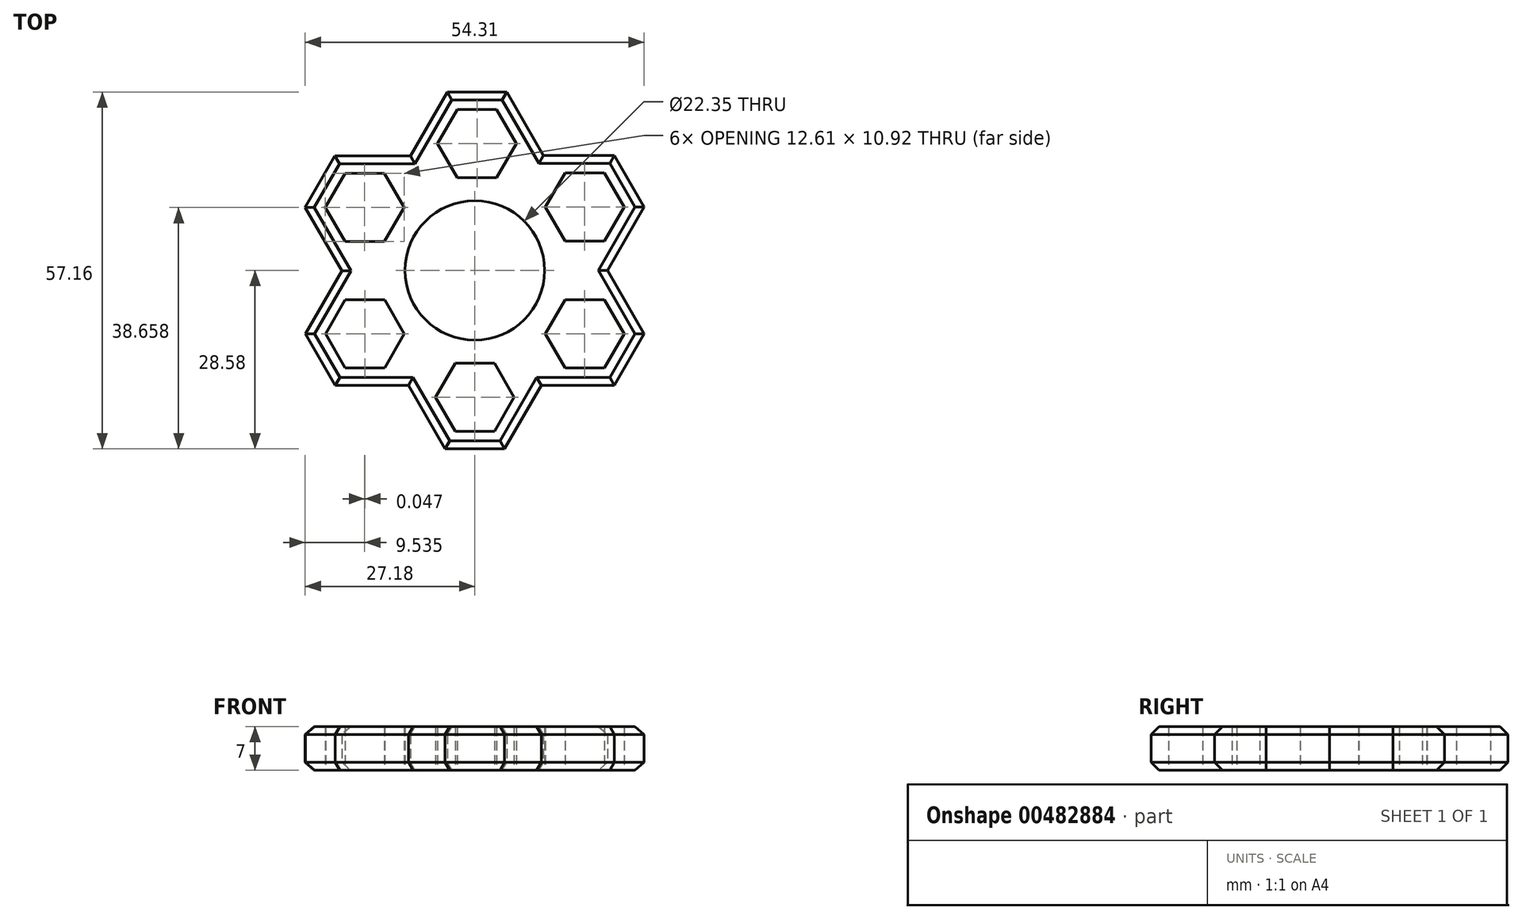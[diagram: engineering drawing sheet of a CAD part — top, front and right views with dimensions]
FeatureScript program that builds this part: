
annotation { "Feature Type Name" : "Feature", "Feature Type Description" : "" }
export const myFeature = defineFeature(function(context is Context, id is Id, definition is map)
    precondition{}
    {
        {
            var Q0;
            Q0=qCreatedBy(makeId("Top.planeOp"),FACE);
            var sketch = newSketch(context, id + "F0", { "sketchPlane" : qUnion([Q0])});
            skCircle(sketch, "E0", {"center": v(0, 0) * mm, "radius": 10.95 * mm});
            skCircle(sketch, "E1.cCircle", {"center": v(0, 0) * mm, "radius": 12.7 * mm, "construction": true});
            skLineSegment(sketch, "E1.0", {"start": v(-7.33, 12.7) * mm, "end": v(7.33, 12.7) * mm});
            skLineSegment(sketch, "E1.1", {"start": v(7.33, 12.7) * mm, "end": v(14.66, 0) * mm});
            skLineSegment(sketch, "E1.2", {"start": v(14.66, 0) * mm, "end": v(7.33, -12.7) * mm});
            skLineSegment(sketch, "E1.3", {"start": v(7.33, -12.7) * mm, "end": v(-7.33, -12.7) * mm});
            skLineSegment(sketch, "E1.4", {"start": v(-7.33, -12.7) * mm, "end": v(-14.66, 0) * mm});
            skLineSegment(sketch, "E1.5", {"start": v(-14.66, 0) * mm, "end": v(-7.33, 12.7) * mm});
            skPoint(sketch, "E1.0.midPoint", {"position": v(0, 12.7) * mm});
            skPoint(sketch, "E2.endSnap0", {"position": v(0, -12.7) * mm});
            skCircle(sketch, "E3.cCircle", {"center": v(0.35, 20.32) * mm, "radius": 5.46 * mm, "construction": true});
            skLineSegment(sketch, "E3.0", {"start": v(3.5, 14.86) * mm, "end": v(-2.8, 14.86) * mm});
            skLineSegment(sketch, "E3.1", {"start": v(-2.8, 14.86) * mm, "end": v(-5.95, 20.32) * mm});
            skLineSegment(sketch, "E3.2", {"start": v(-5.95, 20.32) * mm, "end": v(-2.8, 25.78) * mm});
            skLineSegment(sketch, "E3.3", {"start": v(-2.8, 25.78) * mm, "end": v(3.5, 25.78) * mm});
            skLineSegment(sketch, "E3.4", {"start": v(3.5, 25.78) * mm, "end": v(6.66, 20.32) * mm});
            skLineSegment(sketch, "E3.5", {"start": v(6.66, 20.32) * mm, "end": v(3.5, 14.86) * mm});
            skPoint(sketch, "E3.0.midPoint", {"position": v(0.35, 14.86) * mm});
            skCircle(sketch, "E4.cCircle", {"center": v(17.6, 10.16) * mm, "radius": 5.46 * mm, "construction": true});
            skLineSegment(sketch, "E4.0", {"start": v(14.44, 4.7) * mm, "end": v(11.3, 10.16) * mm});
            skLineSegment(sketch, "E4.1", {"start": v(11.3, 10.16) * mm, "end": v(14.44, 15.62) * mm});
            skLineSegment(sketch, "E4.2", {"start": v(14.44, 15.62) * mm, "end": v(20.75, 15.62) * mm});
            skLineSegment(sketch, "E4.3", {"start": v(20.75, 15.62) * mm, "end": v(23.9, 10.16) * mm});
            skLineSegment(sketch, "E4.4", {"start": v(23.9, 10.16) * mm, "end": v(20.75, 4.7) * mm});
            skLineSegment(sketch, "E4.5", {"start": v(20.75, 4.7) * mm, "end": v(14.44, 4.7) * mm});
            skPoint(sketch, "E4.0.midPoint", {"position": v(12.87, 7.43) * mm});
            skCircle(sketch, "E5.cCircle", {"center": v(17.6, -10.16) * mm, "radius": 5.46 * mm, "construction": true});
            skLineSegment(sketch, "E5.0", {"start": v(11.3, -10.16) * mm, "end": v(14.44, -4.7) * mm});
            skLineSegment(sketch, "E5.1", {"start": v(14.44, -4.7) * mm, "end": v(20.75, -4.7) * mm});
            skLineSegment(sketch, "E5.2", {"start": v(20.75, -4.7) * mm, "end": v(23.9, -10.16) * mm});
            skLineSegment(sketch, "E5.3", {"start": v(23.9, -10.16) * mm, "end": v(20.75, -15.62) * mm});
            skLineSegment(sketch, "E5.4", {"start": v(20.75, -15.62) * mm, "end": v(14.44, -15.62) * mm});
            skLineSegment(sketch, "E5.5", {"start": v(14.44, -15.62) * mm, "end": v(11.3, -10.16) * mm});
            skPoint(sketch, "E5.0.midPoint", {"position": v(12.87, -7.43) * mm});
            skCircle(sketch, "E6.cCircle", {"center": v(0, -20.32) * mm, "radius": 5.46 * mm, "construction": true});
            skLineSegment(sketch, "E6.0", {"start": v(-3.15, -14.86) * mm, "end": v(3.15, -14.86) * mm});
            skLineSegment(sketch, "E6.1", {"start": v(3.15, -14.86) * mm, "end": v(6.3, -20.32) * mm});
            skLineSegment(sketch, "E6.2", {"start": v(6.3, -20.32) * mm, "end": v(3.15, -25.78) * mm});
            skLineSegment(sketch, "E6.3", {"start": v(3.15, -25.78) * mm, "end": v(-3.15, -25.78) * mm});
            skLineSegment(sketch, "E6.4", {"start": v(-3.15, -25.78) * mm, "end": v(-6.3, -20.32) * mm});
            skLineSegment(sketch, "E6.5", {"start": v(-6.3, -20.32) * mm, "end": v(-3.15, -14.86) * mm});
            skPoint(sketch, "E6.0.midPoint", {"position": v(0, -14.86) * mm});
            skCircle(sketch, "E7.cCircle", {"center": v(-17.6, -10.16) * mm, "radius": 5.46 * mm, "construction": true});
            skLineSegment(sketch, "E7.0", {"start": v(-14.44, -4.7) * mm, "end": v(-11.3, -10.16) * mm});
            skLineSegment(sketch, "E7.1", {"start": v(-11.3, -10.16) * mm, "end": v(-14.44, -15.62) * mm});
            skLineSegment(sketch, "E7.2", {"start": v(-14.44, -15.62) * mm, "end": v(-20.75, -15.62) * mm});
            skLineSegment(sketch, "E7.3", {"start": v(-20.75, -15.62) * mm, "end": v(-23.9, -10.16) * mm});
            skLineSegment(sketch, "E7.4", {"start": v(-23.9, -10.16) * mm, "end": v(-20.75, -4.7) * mm});
            skLineSegment(sketch, "E7.5", {"start": v(-20.75, -4.7) * mm, "end": v(-14.44, -4.7) * mm});
            skPoint(sketch, "E7.0.midPoint", {"position": v(-12.87, -7.43) * mm});
            skCircle(sketch, "E8.cCircle", {"center": v(-17.64, 10.08) * mm, "radius": 5.46 * mm, "construction": true});
            skLineSegment(sketch, "E8.0", {"start": v(-11.34, 10.08) * mm, "end": v(-14.5, 4.62) * mm});
            skLineSegment(sketch, "E8.1", {"start": v(-14.5, 4.62) * mm, "end": v(-20.8, 4.62) * mm});
            skLineSegment(sketch, "E8.2", {"start": v(-20.8, 4.62) * mm, "end": v(-23.95, 10.08) * mm});
            skLineSegment(sketch, "E8.3", {"start": v(-23.95, 10.08) * mm, "end": v(-20.8, 15.54) * mm});
            skLineSegment(sketch, "E8.4", {"start": v(-20.8, 15.54) * mm, "end": v(-14.5, 15.54) * mm});
            skLineSegment(sketch, "E8.5", {"start": v(-14.5, 15.54) * mm, "end": v(-11.34, 10.08) * mm});
            skPoint(sketch, "E8.0.midPoint", {"position": v(-12.92, 7.35) * mm});
            skCircle(sketch, "E9.cCircle", {"center": v(-17.64, 10.08) * mm, "radius": 8.26 * mm, "construction": true});
            skLineSegment(sketch, "E9.0", {"start": v(-8.11, 10.08) * mm, "end": v(-12.88, 1.82) * mm});
            skLineSegment(sketch, "E9.1", {"start": v(-12.88, 1.82) * mm, "end": v(-22.41, 1.82) * mm});
            skLineSegment(sketch, "E9.2", {"start": v(-22.41, 1.82) * mm, "end": v(-27.18, 10.08) * mm});
            skLineSegment(sketch, "E9.3", {"start": v(-27.18, 10.08) * mm, "end": v(-22.41, 18.33) * mm});
            skLineSegment(sketch, "E9.4", {"start": v(-22.41, 18.33) * mm, "end": v(-12.88, 18.33) * mm});
            skLineSegment(sketch, "E9.5", {"start": v(-12.88, 18.33) * mm, "end": v(-8.11, 10.08) * mm});
            skPoint(sketch, "E9.0.midPoint", {"position": v(-10.5, 5.95) * mm});
            skCircle(sketch, "E10.cCircle", {"center": v(0.35, 20.32) * mm, "radius": 8.26 * mm, "construction": true});
            skLineSegment(sketch, "E10.0", {"start": v(5.12, 12.06) * mm, "end": v(-4.41, 12.06) * mm});
            skLineSegment(sketch, "E10.1", {"start": v(-4.41, 12.06) * mm, "end": v(-9.18, 20.32) * mm});
            skLineSegment(sketch, "E10.2", {"start": v(-9.18, 20.32) * mm, "end": v(-4.41, 28.58) * mm});
            skLineSegment(sketch, "E10.3", {"start": v(-4.41, 28.58) * mm, "end": v(5.12, 28.58) * mm});
            skLineSegment(sketch, "E10.4", {"start": v(5.12, 28.58) * mm, "end": v(9.89, 20.32) * mm});
            skLineSegment(sketch, "E10.5", {"start": v(9.89, 20.32) * mm, "end": v(5.12, 12.06) * mm});
            skPoint(sketch, "E10.0.midPoint", {"position": v(0.35, 12.06) * mm});
            skCircle(sketch, "E11.cCircle", {"center": v(17.6, 10.16) * mm, "radius": 8.26 * mm, "construction": true});
            skLineSegment(sketch, "E11.0", {"start": v(12.83, 1.9) * mm, "end": v(8.07, 10.16) * mm});
            skLineSegment(sketch, "E11.1", {"start": v(8.07, 10.16) * mm, "end": v(12.83, 18.42) * mm});
            skLineSegment(sketch, "E11.2", {"start": v(12.83, 18.42) * mm, "end": v(22.36, 18.42) * mm});
            skLineSegment(sketch, "E11.3", {"start": v(22.36, 18.42) * mm, "end": v(27.13, 10.16) * mm});
            skLineSegment(sketch, "E11.4", {"start": v(27.13, 10.16) * mm, "end": v(22.36, 1.9) * mm});
            skLineSegment(sketch, "E11.5", {"start": v(22.36, 1.9) * mm, "end": v(12.83, 1.9) * mm});
            skPoint(sketch, "E11.0.midPoint", {"position": v(10.45, 6.03) * mm});
            skCircle(sketch, "E12.cCircle", {"center": v(17.6, -10.16) * mm, "radius": 8.26 * mm, "construction": true});
            skLineSegment(sketch, "E12.0", {"start": v(8.07, -10.16) * mm, "end": v(12.83, -1.9) * mm});
            skLineSegment(sketch, "E12.1", {"start": v(12.83, -1.9) * mm, "end": v(22.36, -1.9) * mm});
            skLineSegment(sketch, "E12.2", {"start": v(22.36, -1.9) * mm, "end": v(27.13, -10.16) * mm});
            skLineSegment(sketch, "E12.3", {"start": v(27.13, -10.16) * mm, "end": v(22.36, -18.41) * mm});
            skLineSegment(sketch, "E12.4", {"start": v(22.36, -18.41) * mm, "end": v(12.83, -18.42) * mm});
            skLineSegment(sketch, "E12.5", {"start": v(12.83, -18.42) * mm, "end": v(8.07, -10.16) * mm});
            skPoint(sketch, "E12.0.midPoint", {"position": v(10.45, -6.03) * mm});
            skCircle(sketch, "E13.cCircle", {"center": v(0, -20.32) * mm, "radius": 8.26 * mm, "construction": true});
            skLineSegment(sketch, "E13.0", {"start": v(-4.77, -12.07) * mm, "end": v(4.77, -12.07) * mm});
            skLineSegment(sketch, "E13.1", {"start": v(4.77, -12.06) * mm, "end": v(9.53, -20.32) * mm});
            skLineSegment(sketch, "E13.2", {"start": v(9.53, -20.32) * mm, "end": v(4.77, -28.58) * mm});
            skLineSegment(sketch, "E13.3", {"start": v(4.77, -28.58) * mm, "end": v(-4.77, -28.58) * mm});
            skLineSegment(sketch, "E13.4", {"start": v(-4.77, -28.58) * mm, "end": v(-9.53, -20.32) * mm});
            skLineSegment(sketch, "E13.5", {"start": v(-9.53, -20.32) * mm, "end": v(-4.77, -12.06) * mm});
            skPoint(sketch, "E13.0.midPoint", {"position": v(0, -12.07) * mm});
            skCircle(sketch, "E14.cCircle", {"center": v(-17.6, -10.16) * mm, "radius": 8.26 * mm, "construction": true});
            skLineSegment(sketch, "E14.0", {"start": v(-12.83, -1.9) * mm, "end": v(-8.07, -10.16) * mm});
            skLineSegment(sketch, "E14.1", {"start": v(-8.07, -10.16) * mm, "end": v(-12.83, -18.42) * mm});
            skLineSegment(sketch, "E14.2", {"start": v(-12.83, -18.42) * mm, "end": v(-22.36, -18.42) * mm});
            skLineSegment(sketch, "E14.3", {"start": v(-22.36, -18.42) * mm, "end": v(-27.13, -10.16) * mm});
            skLineSegment(sketch, "E14.4", {"start": v(-27.13, -10.16) * mm, "end": v(-22.36, -1.9) * mm});
            skLineSegment(sketch, "E14.5", {"start": v(-22.36, -1.9) * mm, "end": v(-12.83, -1.9) * mm});
            skPoint(sketch, "E14.0.midPoint", {"position": v(-10.45, -6.03) * mm});
            skLineSegment(sketch, "E15", {"start": v(-19.93, -1.9) * mm, "end": v(-17.38, -1.9) * mm});
            skLineSegment(sketch, "E16", {"start": v(-7.78, -17.3) * mm, "end": v(-6.51, -15.1) * mm});
            skLineSegment(sketch, "E17", {"start": v(9.81, -13.19) * mm, "end": v(11.08, -15.39) * mm});
            skLineSegment(sketch, "E18", {"start": v(16.33, 1.9) * mm, "end": v(18.87, 1.9) * mm});
            skLineSegment(sketch, "E19", {"start": v(6.91, 15.17) * mm, "end": v(7.1, 15.48) * mm});
            skLineSegment(sketch, "E20.bottom", {"start": v(-1.27, -12.7) * mm, "end": v(1.27, -12.7) * mm});
            skLineSegment(sketch, "E20.top", {"start": v(-1.27, -12.07) * mm, "end": v(1.27, -12.07) * mm});
            skLineSegment(sketch, "E21.bottom", {"start": v(1.27, 12.7) * mm, "end": v(-1.27, 12.7) * mm});
            skLineSegment(sketch, "E21.top", {"start": v(1.27, 12.06) * mm, "end": v(-2, 12.06) * mm});
            skLineSegment(sketch, "E22", {"start": v(10.3, 7.42) * mm, "end": v(9.81, 7.13) * mm});
            skLineSegment(sketch, "E23", {"start": v(10.3, 7.42) * mm, "end": v(11.63, 5.25) * mm});
            skLineSegment(sketch, "E24", {"start": v(11.08, 4.93) * mm, "end": v(11.63, 5.25) * mm});
            skLineSegment(sketch, "E25", {"start": v(11.58, -5.22) * mm, "end": v(11.08, -4.93) * mm});
            skLineSegment(sketch, "E26", {"start": v(11.58, -5.22) * mm, "end": v(10.36, -7.45) * mm});
            skLineSegment(sketch, "E27", {"start": v(9.81, -7.13) * mm, "end": v(10.36, -7.45) * mm});
            skLineSegment(sketch, "E28", {"start": v(-9.81, -7.13) * mm, "end": v(-10.36, -7.45) * mm});
            skLineSegment(sketch, "E29", {"start": v(-9.81, -7.13) * mm, "end": v(-11.08, -4.93) * mm});
            skLineSegment(sketch, "E30", {"start": v(-11.63, -5.25) * mm, "end": v(-11.08, -4.93) * mm});
            skLineSegment(sketch, "E31", {"start": v(-10.63, 5.72) * mm, "end": v(-11.18, 6.04) * mm});
            skLineSegment(sketch, "E32", {"start": v(-10.63, 5.72) * mm, "end": v(-9.31, 8) * mm});
            skLineSegment(sketch, "E33", {"start": v(-9.86, 8.32) * mm, "end": v(-9.31, 8) * mm});
            skLineSegment(sketch, "E34", {"start": v(-11.18, 6.04) * mm, "end": v(-9.86, 8.32) * mm});
            skLineSegment(sketch, "E35", {"start": v(-9.31, 8) * mm, "end": v(-10.63, 5.72) * mm});
            skLineSegment(sketch, "E36", {"start": v(11.08, 4.93) * mm, "end": v(9.81, 7.13) * mm});
            skLineSegment(sketch, "E37", {"start": v(-11.08, -4.93) * mm, "end": v(-11.63, -5.25) * mm});
            skLineSegment(sketch, "E38", {"start": v(-11.08, -4.93) * mm, "end": v(-9.81, -7.13) * mm});
            skLineSegment(sketch, "E39", {"start": v(-10.36, -7.45) * mm, "end": v(-9.81, -7.13) * mm});
            skLineSegment(sketch, "E40", {"start": v(-10.36, -7.45) * mm, "end": v(-11.63, -5.25) * mm});
            skCircle(sketch, "E41", {"center": v(0, 0) * mm, "radius": 11.08 * mm});
            skCircle(sketch, "E42", {"center": v(0, 0) * mm, "radius": 11.07 * mm});
            skLineSegment(sketch, "E43", {"start": v(-4.77, -28.58) * mm, "end": v(-10.63, -18.42) * mm});
            skLineSegment(sketch, "E44", {"start": v(-10.63, -18.42) * mm, "end": v(-22.36, -18.42) * mm});
            skLineSegment(sketch, "E45", {"start": v(-27.13, -10.16) * mm, "end": v(-21.26, 0) * mm});
            skLineSegment(sketch, "E46", {"start": v(-27.18, 10.08) * mm, "end": v(-21.26, -0.16) * mm});
            skLineSegment(sketch, "E47", {"start": v(-22.41, 18.33) * mm, "end": v(-9.9, 18.33) * mm});
            skLineSegment(sketch, "E48", {"start": v(-4.41, 28.58) * mm, "end": v(-10.68, 17.72) * mm});
            skLineSegment(sketch, "E49", {"start": v(5.12, 28.58) * mm, "end": v(11.52, 17.5) * mm});
            skLineSegment(sketch, "E50", {"start": v(22.36, 18.42) * mm, "end": v(9.92, 18.42) * mm});
            skLineSegment(sketch, "E51", {"start": v(27.13, 10.16) * mm, "end": v(20.6, -1.15) * mm});
            skLineSegment(sketch, "E52", {"start": v(22.36, -18.41) * mm, "end": v(10.34, -18.41) * mm});
            skLineSegment(sketch, "E53", {"start": v(4.77, -28.58) * mm, "end": v(11, -17.8) * mm});
            skLineSegment(sketch, "E54", {"start": v(27.13, -10.16) * mm, "end": v(20.86, 0.7) * mm});
            skSolve(sketch);
        }
        {
            var Q0;
            Q0=qSketchRegion(id+"F0",true);
            var Q1;
            Q1=makeQuery(id+"F0.imprint","IMPRINT",FACE,{"disambiguationData":[TD([[makeQuery(id+"F0.imprint","IMPRINT",EDGE,{"derivedFrom":sQuery(id+"F0.wireOp",EDGE,"E21.bottom")}),-1.0]])]});
            var Q2;
            Q2=makeQuery(id+"F0.imprint","IMPRINT",FACE,{"disambiguationData":[TD([[makeQuery(id+"F0.imprint","IMPRINT",EDGE,{"derivedFrom":sQuery(id+"F0.wireOp",EDGE,"E37")}),1.0]])]});
            var Q3;
            Q3=makeQuery(id+"F0.imprint","IMPRINT",FACE,{"disambiguationData":[TD([[makeQuery(id+"F0.imprint","IMPRINT",EDGE,{"derivedFrom":sQuery(id+"F0.wireOp",EDGE,"E20.bottom")}),-1.0]])]});
            var Q4;
            {var subQ0=sQuery(id+"F0.wireOp",EDGE,"E27");Q4=makeQuery(id+"F0.imprint","IMPRINT",FACE,{"disambiguationData":[TD([[makeQuery(id+"F0.imprint","IMPRINT",EDGE,{"derivedFrom":subQ0}),1.0]])]});}
            var Q5;
            {var subQ0=sQuery(id+"F0.wireOp",EDGE,"E24");Q5=makeQuery(id+"F0.imprint","IMPRINT",FACE,{"disambiguationData":[TD([[makeQuery(id+"F0.imprint","IMPRINT",EDGE,{"derivedFrom":subQ0}),1.0]])]});}
            var Q6;
            Q6=makeQuery(id+"F0.imprint","IMPRINT",FACE,{"disambiguationData":[TD([[makeQuery(id+"F0.imprint","IMPRINT",EDGE,{"derivedFrom":sQuery(id+"F0.wireOp",EDGE,"E33")}),-1.0]])]});
            var Q7;
            {var subQ1=sQuery(id+"F0.wireOp",EDGE,"E22");Q7=makeQuery(id+"F0.imprint","IMPRINT",FACE,{"disambiguationData":[TD([[makeQuery(id+"F0.imprint","IMPRINT",EDGE,{"derivedFrom":subQ1}),-1.0]])]});}
            var Q8;
            {var subQ1=sQuery(id+"F0.wireOp",EDGE,"E25");Q8=makeQuery(id+"F0.imprint","IMPRINT",FACE,{"disambiguationData":[TD([[makeQuery(id+"F0.imprint","IMPRINT",EDGE,{"derivedFrom":subQ1}),-1.0]])]});}
            extrude(context, id + "F1", {"entities" : qUnion([Q0, Q1, Q2, Q3, Q4, Q5, Q6, Q7, Q8]), "depth" : 7 * mm});
        }
        {
            var Q0;
            Q0=qCreatedBy(makeId("Top.planeOp"),FACE);
            var sketch = newSketch(context, id + "F2", { "sketchPlane" : qUnion([Q0])});
            skCircle(sketch, "E55", {"center": v(0, 0) * mm, "radius": 11.18 * mm});
            skCircle(sketch, "E56.cCircle", {"center": v(0, 0) * mm, "radius": 13.34 * mm, "construction": true});
            skLineSegment(sketch, "E56.0", {"start": v(-7.7, 13.33) * mm, "end": v(7.7, 13.34) * mm});
            skLineSegment(sketch, "E56.1", {"start": v(7.7, 13.34) * mm, "end": v(15.4, 0) * mm});
            skLineSegment(sketch, "E56.2", {"start": v(15.4, 0) * mm, "end": v(7.7, -13.33) * mm});
            skLineSegment(sketch, "E56.3", {"start": v(7.7, -13.33) * mm, "end": v(-7.7, -13.34) * mm});
            skLineSegment(sketch, "E56.4", {"start": v(-7.7, -13.34) * mm, "end": v(-15.4, 0) * mm});
            skLineSegment(sketch, "E56.5", {"start": v(-15.4, 0) * mm, "end": v(-7.7, 13.33) * mm});
            skPoint(sketch, "E56.0.midPoint", {"position": v(0, 13.33) * mm});
            skSolve(sketch);
        }
        {
            var Q0;
            Q0=qSketchRegion(id+"F2",true);
            extrude(context, id + "F3", {"entities" : qUnion([Q0]), "operationType" : NewBodyOperationType.ADD, "depth" : 7 * mm});
        }
        {
            var Q0;
            Q0=makeQuery(id+"F1.opExtrude","CAP_EDGE",EDGE,{"disambiguationData":[OSD([sQuery(id+"F0.wireOp",EDGE,"E44")])],"isStart":false});
            var Q1;
            Q1=makeQuery(id+"F1.opExtrude","CAP_EDGE",EDGE,{"disambiguationData":[OSD([sQuery(id+"F0.wireOp",EDGE,"E44")])],"isStart":true});
            var Q2;
            Q2=makeQuery(id+"F1.opExtrude","CAP_EDGE",EDGE,{"disambiguationData":[OSD([sQuery(id+"F0.wireOp",EDGE,"E43")])],"isStart":false});
            var Q3;
            Q3=makeQuery(id+"F1.opExtrude","CAP_EDGE",EDGE,{"disambiguationData":[OSD([sQuery(id+"F0.wireOp",EDGE,"E43")])],"isStart":true});
            var Q4;
            Q4=makeQuery(id+"F1.opExtrude","CAP_EDGE",EDGE,{"disambiguationData":[OSD([sQuery(id+"F0.wireOp",EDGE,"E13.3")])],"isStart":false});
            var Q5;
            Q5=makeQuery(id+"F1.opExtrude","CAP_EDGE",EDGE,{"disambiguationData":[OSD([sQuery(id+"F0.wireOp",EDGE,"E13.3")])],"isStart":true});
            var Q6;
            Q6=makeQuery(id+"F1.opExtrude","CAP_EDGE",EDGE,{"disambiguationData":[OSD([sQuery(id+"F0.wireOp",EDGE,"E53")])],"isStart":true});
            var Q7;
            Q7=makeQuery(id+"F1.opExtrude","CAP_EDGE",EDGE,{"disambiguationData":[OSD([sQuery(id+"F0.wireOp",EDGE,"E53")])],"isStart":false});
            var Q8;
            Q8=makeQuery(id+"F1.opExtrude","CAP_EDGE",EDGE,{"disambiguationData":[OSD([sQuery(id+"F0.wireOp",EDGE,"E52")])],"isStart":true});
            var Q9;
            Q9=makeQuery(id+"F1.opExtrude","CAP_EDGE",EDGE,{"disambiguationData":[OSD([sQuery(id+"F0.wireOp",EDGE,"E52")])],"isStart":false});
            var Q10;
            Q10=makeQuery(id+"F1.opExtrude","CAP_EDGE",EDGE,{"disambiguationData":[OSD([sQuery(id+"F0.wireOp",EDGE,"E12.3")])],"isStart":false});
            var Q11;
            Q11=makeQuery(id+"F1.opExtrude","CAP_EDGE",EDGE,{"disambiguationData":[OSD([sQuery(id+"F0.wireOp",EDGE,"E12.3")])],"isStart":true});
            var Q12;
            Q12=makeQuery(id+"F1.opExtrude","CAP_EDGE",EDGE,{"disambiguationData":[OSD([sQuery(id+"F0.wireOp",EDGE,"vZolWrX7-FvXN-jlpN-AbtS-Bu0TkdeIzU0z")])],"isStart":false});
            var Q13;
            Q13=makeQuery(id+"F1.opExtrude","CAP_EDGE",EDGE,{"disambiguationData":[OSD([sQuery(id+"F0.wireOp",EDGE,"vZolWrX7-FvXN-jlpN-AbtS-Bu0TkdeIzU0z")])],"isStart":true});
            var Q14;
            Q14=makeQuery(id+"F1.opExtrude","CAP_EDGE",EDGE,{"disambiguationData":[OSD([sQuery(id+"F0.wireOp",EDGE,"E51")])],"isStart":true});
            var Q15;
            Q15=makeQuery(id+"F1.opExtrude","CAP_EDGE",EDGE,{"disambiguationData":[OSD([sQuery(id+"F0.wireOp",EDGE,"E51")])],"isStart":false});
            var Q16;
            Q16=makeQuery(id+"F1.opExtrude","CAP_EDGE",EDGE,{"disambiguationData":[OSD([sQuery(id+"F0.wireOp",EDGE,"E11.3")])],"isStart":false});
            var Q17;
            Q17=makeQuery(id+"F1.opExtrude","CAP_EDGE",EDGE,{"disambiguationData":[OSD([sQuery(id+"F0.wireOp",EDGE,"E11.3")])],"isStart":true});
            var Q18;
            Q18=makeQuery(id+"F1.opExtrude","CAP_EDGE",EDGE,{"disambiguationData":[OSD([sQuery(id+"F0.wireOp",EDGE,"E50")])],"isStart":true});
            var Q19;
            Q19=makeQuery(id+"F1.opExtrude","CAP_EDGE",EDGE,{"disambiguationData":[OSD([sQuery(id+"F0.wireOp",EDGE,"E50")])],"isStart":false});
            var Q20;
            Q20=makeQuery(id+"F1.opExtrude","CAP_EDGE",EDGE,{"disambiguationData":[OSD([sQuery(id+"F0.wireOp",EDGE,"E49")])],"isStart":true});
            var Q21;
            Q21=makeQuery(id+"F1.opExtrude","CAP_EDGE",EDGE,{"disambiguationData":[OSD([sQuery(id+"F0.wireOp",EDGE,"E49")])],"isStart":false});
            var Q22;
            Q22=makeQuery(id+"F1.opExtrude","CAP_EDGE",EDGE,{"disambiguationData":[OSD([sQuery(id+"F0.wireOp",EDGE,"E10.3")])],"isStart":true});
            var Q23;
            Q23=makeQuery(id+"F1.opExtrude","CAP_EDGE",EDGE,{"disambiguationData":[OSD([sQuery(id+"F0.wireOp",EDGE,"E10.3")])],"isStart":false});
            var Q24;
            Q24=makeQuery(id+"F1.opExtrude","CAP_EDGE",EDGE,{"disambiguationData":[OSD([sQuery(id+"F0.wireOp",EDGE,"E48")])],"isStart":false});
            var Q25;
            Q25=makeQuery(id+"F1.opExtrude","CAP_EDGE",EDGE,{"disambiguationData":[OSD([sQuery(id+"F0.wireOp",EDGE,"E48")])],"isStart":true});
            var Q26;
            Q26=makeQuery(id+"F1.opExtrude","CAP_EDGE",EDGE,{"disambiguationData":[OSD([sQuery(id+"F0.wireOp",EDGE,"E47")])],"isStart":true});
            var Q27;
            Q27=makeQuery(id+"F1.opExtrude","CAP_EDGE",EDGE,{"disambiguationData":[OSD([sQuery(id+"F0.wireOp",EDGE,"E47")])],"isStart":false});
            var Q28;
            Q28=makeQuery(id+"F1.opExtrude","CAP_EDGE",EDGE,{"disambiguationData":[OSD([sQuery(id+"F0.wireOp",EDGE,"E9.3")])],"isStart":true});
            var Q29;
            Q29=makeQuery(id+"F1.opExtrude","CAP_EDGE",EDGE,{"disambiguationData":[OSD([sQuery(id+"F0.wireOp",EDGE,"E9.3")])],"isStart":false});
            var Q30;
            Q30=makeQuery(id+"F1.opExtrude","CAP_EDGE",EDGE,{"disambiguationData":[OSD([sQuery(id+"F0.wireOp",EDGE,"E46")])],"isStart":false});
            var Q31;
            Q31=makeQuery(id+"F1.opExtrude","CAP_EDGE",EDGE,{"disambiguationData":[OSD([sQuery(id+"F0.wireOp",EDGE,"E46")])],"isStart":true});
            var Q32;
            Q32=makeQuery(id+"F1.opExtrude","CAP_EDGE",EDGE,{"disambiguationData":[OSD([sQuery(id+"F0.wireOp",EDGE,"E45")])],"isStart":true});
            var Q33;
            Q33=makeQuery(id+"F1.opExtrude","CAP_EDGE",EDGE,{"disambiguationData":[OSD([sQuery(id+"F0.wireOp",EDGE,"E45")])],"isStart":false});
            var Q34;
            Q34=makeQuery(id+"F1.opExtrude","CAP_EDGE",EDGE,{"disambiguationData":[OSD([sQuery(id+"F0.wireOp",EDGE,"E14.3")])],"isStart":false});
            var Q35;
            Q35=makeQuery(id+"F1.opExtrude","CAP_EDGE",EDGE,{"disambiguationData":[OSD([sQuery(id+"F0.wireOp",EDGE,"E14.3")])],"isStart":true});
            var Q36;
            Q36=makeQuery(id+"F1.opExtrude","CAP_EDGE",EDGE,{"disambiguationData":[OSD([sQuery(id+"F0.wireOp",EDGE,"E54")])],"isStart":true});
            var Q37;
            Q37=makeQuery(id+"F1.opExtrude","CAP_EDGE",EDGE,{"disambiguationData":[OSD([sQuery(id+"F0.wireOp",EDGE,"E54")])],"isStart":false});
            chamfer(context, id + "F4", {"entities" : qUnion([Q0, Q1, Q2, Q3, Q4, Q5, Q6, Q7, Q8, Q9, Q10, Q11, Q12, Q13, Q14, Q15, Q16, Q17, Q18, Q19, Q20, Q21, Q22, Q23, Q24, Q25, Q26, Q27, Q28, Q29, Q30, Q31, Q32, Q33, Q34, Q35, Q36, Q37]), "width" : 1.27 * mm, "tangentPropagation" : true});
        }
    });
